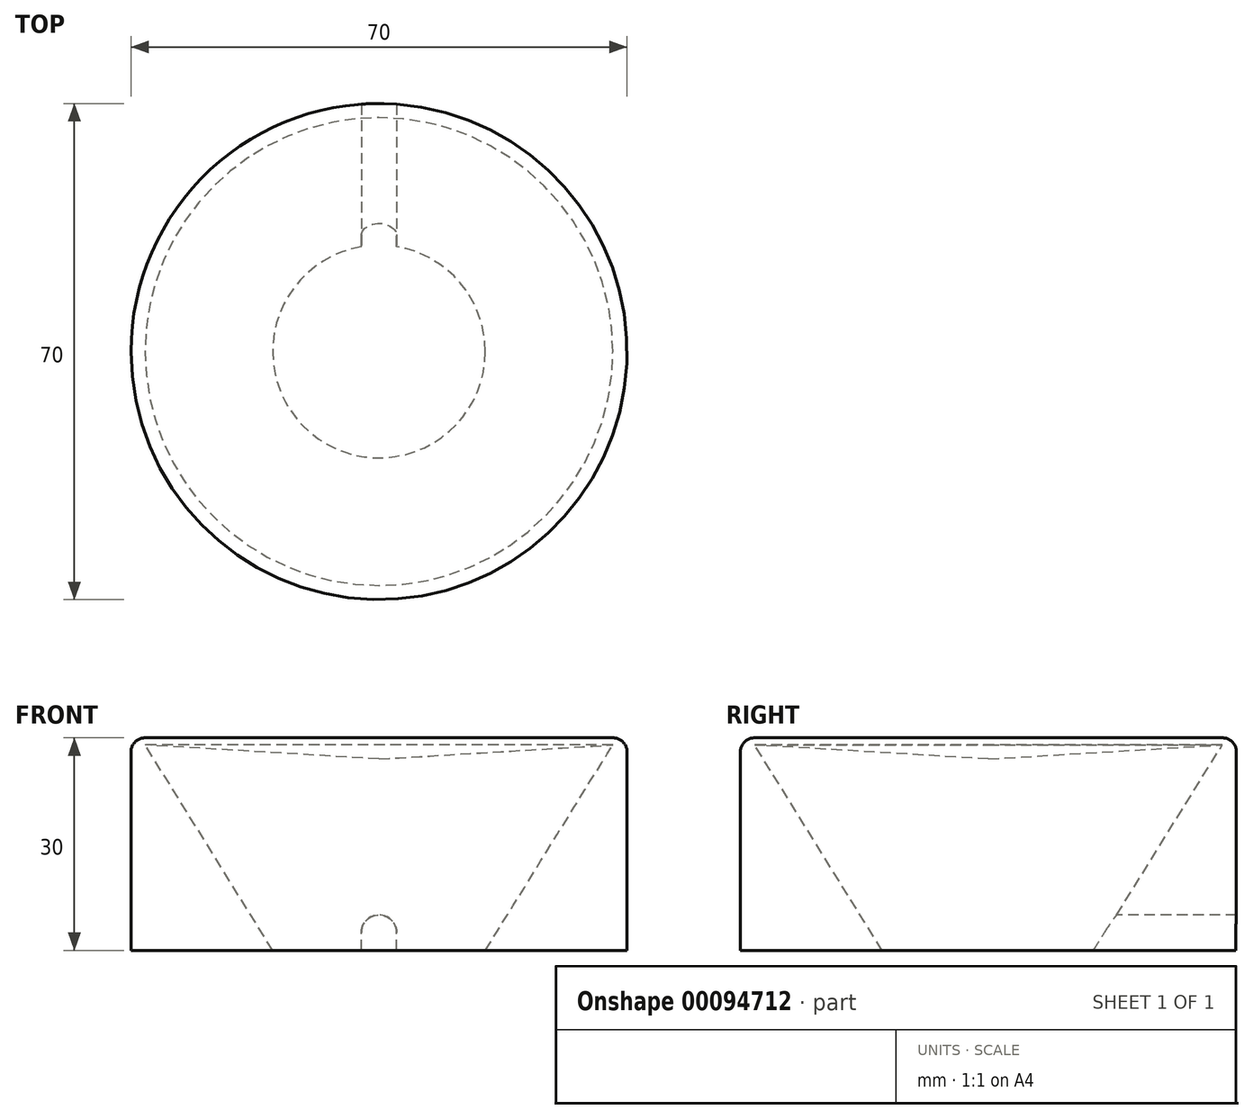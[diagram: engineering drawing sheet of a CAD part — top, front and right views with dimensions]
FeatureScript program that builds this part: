
annotation { "Feature Type Name" : "Feature", "Feature Type Description" : "" }
export const myFeature = defineFeature(function(context is Context, id is Id, definition is map)
    precondition{}
    {
        {
            var Q0;
            Q0=qCreatedBy(makeId("Front.planeOp"),FACE);
            var sketch = newSketch(context, id + "F0", { "sketchPlane" : qUnion([Q0])});
            skLineSegment(sketch, "E0", {"start": v(0, 14.8) * mm, "end": v(0, 11.8) * mm});
            skLineSegment(sketch, "E1", {"start": v(0, 11.8) * mm, "end": v(33, 13.8) * mm});
            skLineSegment(sketch, "E2", {"start": v(33, 13.8) * mm, "end": v(15, -15.2) * mm});
            skLineSegment(sketch, "E3", {"start": v(15, -15.2) * mm, "end": v(35, -15.2) * mm});
            skLineSegment(sketch, "E4", {"start": v(35, -15.2) * mm, "end": v(35, 14.8) * mm});
            skLineSegment(sketch, "E5", {"start": v(35, 14.8) * mm, "end": v(0, 14.8) * mm});
            skSolve(sketch);
        }
        {
            var Q0;
            Q0 = qSketchRegion(id + "F0", true);
            var Q1;
            Q1=sQuery(id+"F0.wireOp",EDGE,"E0");
            revolve(context, id + "F1", {"entities" : qUnion([Q0]), "axis" : qUnion([Q1]), "revolveType" : RevolveType.FULL});
        }
        {
            var Q0;
            Q0=makeQuery(id+"F1.opRevolve","SWEPT_EDGE",EDGE,{"disambiguationData":[OSD([sQuery(id+"F0.wireOp",EDGE,"E4"),sQuery(id+"F0.wireOp",EDGE,"E5")])]});
            fillet(context, id + "F2", {"entities" : qUnion([Q0]), "radius" : 2 * mm, "tangentPropagation" : true, "allowEdgeOverflow" : false});
        }
        {
            var Q0;
            Q0=qCreatedBy(makeId("Front.planeOp"),FACE);
            var sketch = newSketch(context, id + "F3", { "sketchPlane" : qUnion([Q0])});
            skLineSegment(sketch, "E6", {"start": v(0, 0) * mm, "end": v(0, -36.64) * mm, "construction": true});
            skCircle(sketch, "E7", {"center": v(0, -12.7) * mm, "radius": 2.5 * mm});
            skLineSegment(sketch, "E8.bottom", {"start": v(2.5, -12.7) * mm, "end": v(-2.5, -12.7) * mm});
            skLineSegment(sketch, "E8.top", {"start": v(2.5, -17.7) * mm, "end": v(-2.5, -17.7) * mm});
            skLineSegment(sketch, "E8.left", {"start": v(2.5, -12.7) * mm, "end": v(2.5, -17.7) * mm});
            skLineSegment(sketch, "E8.right", {"start": v(-2.5, -12.7) * mm, "end": v(-2.5, -17.7) * mm});
            skPoint(sketch, "E8.middle", {"position": v(0, -15.2) * mm});
            skSolve(sketch);
        }
        {
            var Q0;
            Q0 = qSketchRegion(id + "F3", true);
            extrude(context, id + "F4", {"entities" : qUnion([Q0]), "operationType" : NewBodyOperationType.REMOVE, "oppositeDirection" : true, "depth" : 50 * mm});
        }
    });
